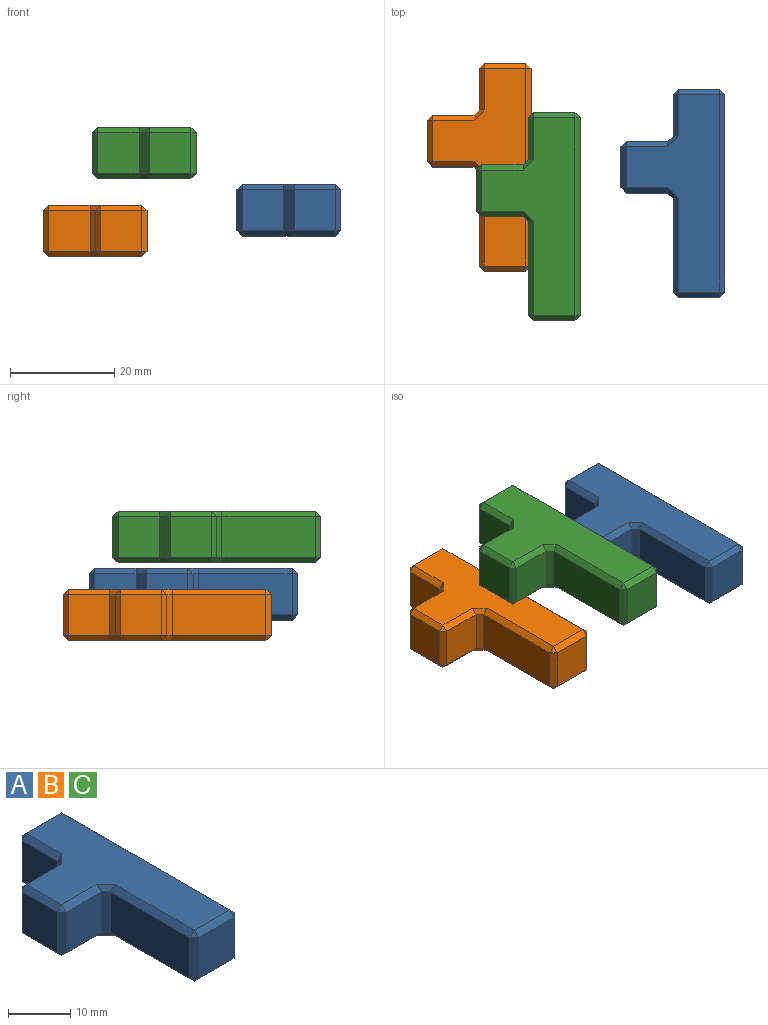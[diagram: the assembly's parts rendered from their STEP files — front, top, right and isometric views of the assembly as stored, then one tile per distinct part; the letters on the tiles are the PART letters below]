
ASSEMBLY  parts=3 mates=1
PART A: 50 faces, bbox 20x40x10 mm
  f0: plane 38.02x17.98mm, normal (0,0,1), area 386.4mm2, adj f10,f11,f14,f15,f24,f25,f30,f34
  f1: plane 38.02x17.98mm, normal (0,0,-1), area 386.4mm2, adj f17,f18,f22,f27,f32,f38,f42,f43
  f2: plane 8.02x7.96mm, normal (-1,0,0), area 63.8mm2, adj f36,f37,f45,f46
  f3: plane 7.96x7.96mm, normal (0,-1,0), area 63.4mm2, adj f23,f24,f32,f33
  f4: plane 38.02x7.96mm, normal (1,0,0), area 302.6mm2, adj f33,f34,f43,f44
  f5: plane 18.04x7.96mm, normal (-1,0,0), area 143.6mm2, adj f13,f14,f22,f23
  f6: plane 7.96x7.96mm, normal (0,1,0), area 63.4mm2, adj f35,f44,f45,f49
  f7: plane 8.02x7.96mm, normal (0,-1,0), area 63.8mm2, adj f10,f13,f16,f17
  f8: plane 8.02x7.96mm, normal (0,1,0), area 63.8mm2, adj f25,f26,f37,f38
  f9: plane 7.96x7.96mm, normal (-1,0,0), area 63.4mm2, adj f15,f16,f26,f27
  f10: plane 8.02x1mm, normal (0,-0.71,0.71), area 11.3mm2, adj f0,f7,f11,f12
  f11: plane 2x2mm, normal (-0.58,-0.58,0.58), area 2.6mm2, adj f0,f10,f13,f14
  f12: plane 1x1mm, normal (-0.58,-0.58,0.58), area 0.9mm2, adj f10,f15,f16
  f13: plane 7.96x1mm, normal (-0.71,-0.71,0), area 11.3mm2, adj f5,f7,f11,f18
  f14: plane 18.04x1mm, normal (-0.71,0,0.71), area 25.5mm2, adj f0,f5,f11,f19
  f15: plane 7.96x1mm, normal (-0.71,0,0.71), area 11.3mm2, adj f0,f9,f12,f20
  f16: plane 7.96x1mm, normal (-0.71,-0.71,0), area 11.3mm2, adj f7,f9,f12,f21
  f17: plane 8.02x1mm, normal (0,-0.71,-0.71), area 11.3mm2, adj f1,f7,f18,f21
  f18: plane 2x2mm, normal (-0.58,-0.58,-0.58), area 2.6mm2, adj f1,f13,f17,f22
  f19: plane 1x1mm, normal (-0.58,-0.58,0.58), area 0.9mm2, adj f14,f23,f24
  f20: plane 1x1mm, normal (-0.58,0.58,0.58), area 0.9mm2, adj f15,f25,f26
  f21: plane 1x1mm, normal (-0.58,-0.58,-0.58), area 0.9mm2, adj f16,f17,f27
  f22: plane 18.04x1mm, normal (-0.71,0,-0.71), area 25.5mm2, adj f1,f5,f18,f28
  f23: plane 7.96x1mm, normal (-0.71,-0.71,0), area 11.3mm2, adj f3,f5,f19,f28
  f24: plane 7.96x1mm, normal (0,-0.71,0.71), area 11.3mm2, adj f0,f3,f19,f29
  f25: plane 8.02x1mm, normal (0,0.71,0.71), area 11.3mm2, adj f0,f8,f20,f30
  f26: plane 7.96x1mm, normal (-0.71,0.71,0), area 11.3mm2, adj f8,f9,f20,f31
  f27: plane 7.96x1mm, normal (-0.71,0,-0.71), area 11.3mm2, adj f1,f9,f21,f31
  f28: plane 1x1mm, normal (-0.58,-0.58,-0.58), area 0.9mm2, adj f22,f23,f32
  f29: plane 1x1mm, normal (0.58,-0.58,0.58), area 0.9mm2, adj f24,f33,f34
  f30: plane 2x2mm, normal (-0.58,0.58,0.58), area 2.6mm2, adj f0,f25,f36,f37
  f31: plane 1x1mm, normal (-0.58,0.58,-0.58), area 0.9mm2, adj f26,f27,f38
  f32: plane 7.96x1mm, normal (0,-0.71,-0.71), area 11.3mm2, adj f1,f3,f28,f39
  f33: plane 7.96x1mm, normal (0.71,-0.71,0), area 11.3mm2, adj f3,f4,f29,f39
  f34: plane 38.02x1mm, normal (0.71,0,0.71), area 53.8mm2, adj f0,f4,f29,f40
  f35: plane 7.96x1mm, normal (0,0.71,0.71), area 11.3mm2, adj f0,f6,f40,f41
  f36: plane 8.02x1mm, normal (-0.71,0,0.71), area 11.3mm2, adj f0,f2,f30,f41
  f37: plane 7.96x1mm, normal (-0.71,0.71,0), area 11.3mm2, adj f2,f8,f30,f42
  f38: plane 8.02x1mm, normal (0,0.71,-0.71), area 11.3mm2, adj f1,f8,f31,f42
  f39: plane 1x1mm, normal (0.58,-0.58,-0.58), area 0.9mm2, adj f32,f33,f43
  f40: plane 1x1mm, normal (0.58,0.58,0.58), area 0.9mm2, adj f34,f35,f44
  f41: plane 1x1mm, normal (-0.58,0.58,0.58), area 0.9mm2, adj f35,f36,f45
  f42: plane 2x2mm, normal (-0.58,0.58,-0.58), area 2.6mm2, adj f1,f37,f38,f46
  f43: plane 38.02x1mm, normal (0.71,0,-0.71), area 53.8mm2, adj f1,f4,f39,f47
  f44: plane 7.96x1mm, normal (0.71,0.71,0), area 11.3mm2, adj f4,f6,f40,f47
  f45: plane 7.96x1mm, normal (-0.71,0.71,0), area 11.3mm2, adj f2,f6,f41,f48
  f46: plane 8.02x1mm, normal (-0.71,0,-0.71), area 11.3mm2, adj f1,f2,f42,f48
  f47: plane 1x1mm, normal (0.58,0.58,-0.58), area 0.9mm2, adj f43,f44,f49
  f48: plane 1x1mm, normal (-0.58,0.58,-0.58), area 0.9mm2, adj f45,f46,f49
  f49: plane 7.96x1mm, normal (0,0.71,-0.71), area 11.3mm2, adj f1,f6,f47,f48
PART B: same geometry as A
PART C: same geometry as A
PLACE A t=(9.53,-21.12,-7.12)mm
PLACE B t=(-27.74,-16.11,-11.1)mm
PLACE C t=(-18.3,-25.67,3.87)mm
MATE slider B.f4 <-> A.f9  axis (1,0,0) through (-22.76,-1.08,-7.12)mm
